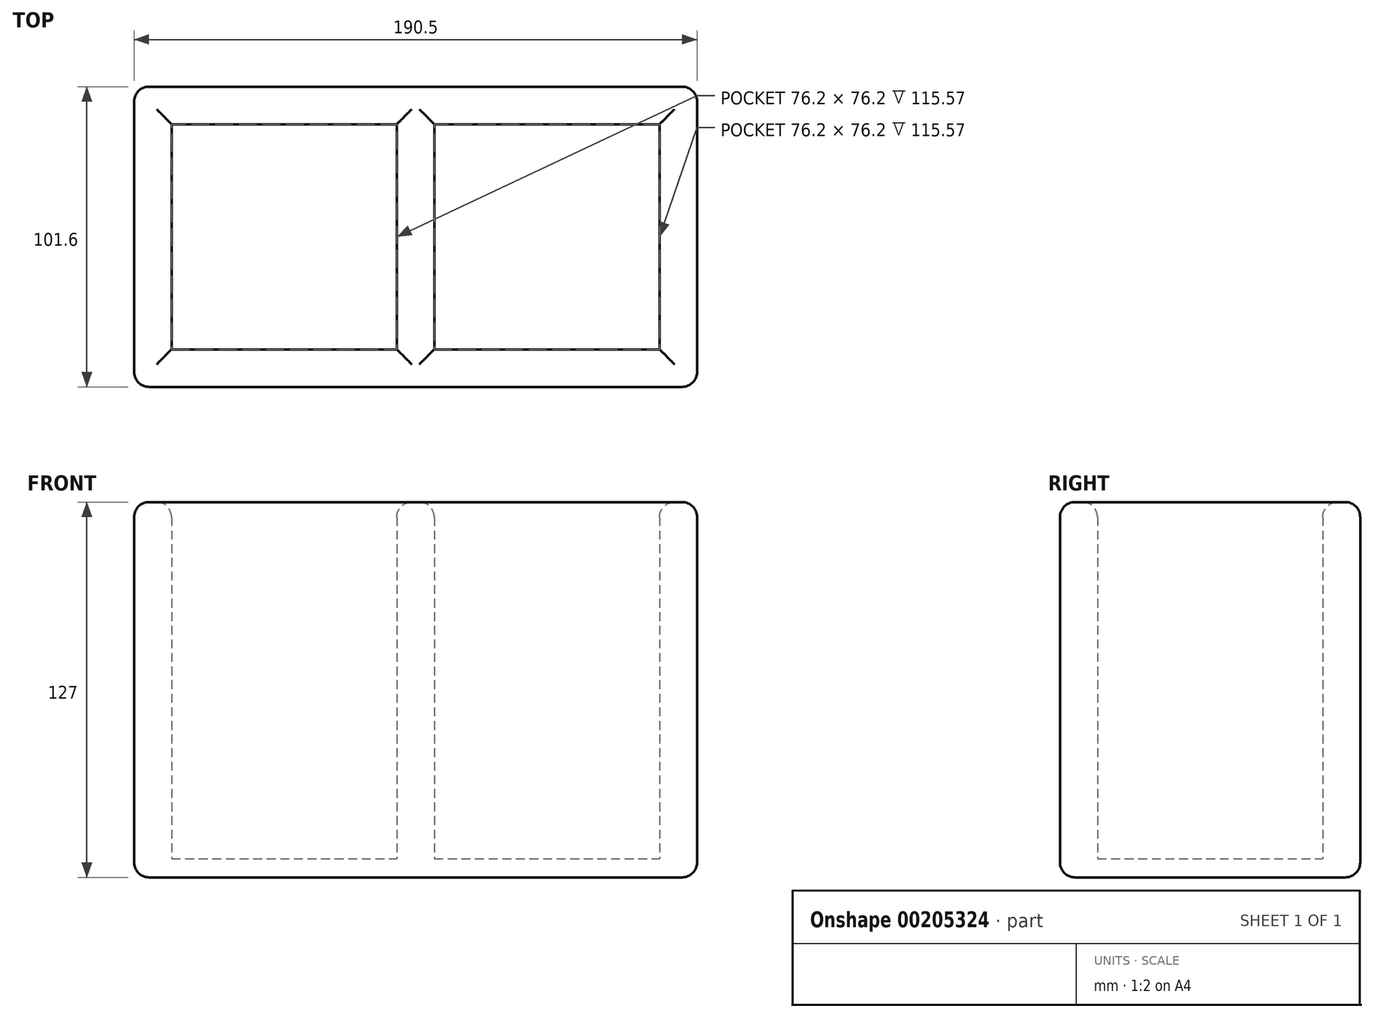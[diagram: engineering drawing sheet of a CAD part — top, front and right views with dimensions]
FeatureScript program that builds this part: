
annotation { "Feature Type Name" : "Feature", "Feature Type Description" : "" }
export const myFeature = defineFeature(function(context is Context, id is Id, definition is map)
    precondition{}
    {
        {
            var Q0;
            Q0=qCreatedBy(makeId("Top.planeOp"),FACE);
            var sketch = newSketch(context, id + "F0", { "sketchPlane" : qUnion([Q0])});
            skLineSegment(sketch, "E0.bottom", {"start": v(-95.25, -50.8) * mm, "end": v(95.25, -50.8) * mm});
            skLineSegment(sketch, "E0.top", {"start": v(-95.25, 50.8) * mm, "end": v(95.25, 50.8) * mm});
            skLineSegment(sketch, "E0.left", {"start": v(-95.25, -50.8) * mm, "end": v(-95.25, 50.8) * mm});
            skLineSegment(sketch, "E0.right", {"start": v(95.25, -50.8) * mm, "end": v(95.25, 50.8) * mm});
            skPoint(sketch, "E0.middle", {"position": v(0, 0) * mm});
            skLineSegment(sketch, "E1.0", {"start": v(-82.55, 38.1) * mm, "end": v(-6.35, 38.1) * mm});
            skLineSegment(sketch, "E1.1", {"start": v(-82.55, -38.1) * mm, "end": v(-82.55, 38.1) * mm});
            skLineSegment(sketch, "E1.2", {"start": v(-82.55, -38.1) * mm, "end": v(-6.35, -38.1) * mm});
            skLineSegment(sketch, "E1.3", {"start": v(82.55, -38.1) * mm, "end": v(82.55, 38.1) * mm});
            skPoint(sketch, "E2", {"position": v(-6.35, -38.1) * mm});
            skPoint(sketch, "E3", {"position": v(6.35, -38.1) * mm});
            skLineSegment(sketch, "E4", {"start": v(-6.35, -38.1) * mm, "end": v(-6.35, 38.1) * mm});
            skLineSegment(sketch, "E5", {"start": v(6.35, -38.1) * mm, "end": v(6.35, 38.1) * mm});
            skLineSegment(sketch, "E6.trimOffspring", {"start": v(6.35, 38.1) * mm, "end": v(82.55, 38.1) * mm});
            skLineSegment(sketch, "E7.trimOffspring", {"start": v(6.35, -38.1) * mm, "end": v(82.55, -38.1) * mm});
            skSolve(sketch);
        }
        {
            var Q0;
            Q0=makeQuery(id+"F0.imprint","IMPRINT",FACE,{"disambiguationData":[TD([[makeQuery(id+"F0.imprint","IMPRINT",EDGE,{"derivedFrom":sQuery(id+"F0.wireOp",EDGE,"E0.bottom")}),1.0]])]});
            extrude(context, id + "F1", {"entities" : qUnion([Q0]), "depth" : 127 * mm});
        }
        {
            var Q0;
            Q0=makeQuery(id+"F0.imprint","IMPRINT",FACE,{"disambiguationData":[TD([[makeQuery(id+"F0.imprint","IMPRINT",EDGE,{"derivedFrom":sQuery(id+"F0.wireOp",EDGE,"E1.0")}),-1.0]])]});
            var Q1;
            Q1=makeQuery(id+"F0.imprint","IMPRINT",FACE,{"disambiguationData":[TD([[makeQuery(id+"F0.imprint","IMPRINT",EDGE,{"derivedFrom":sQuery(id+"F0.wireOp",EDGE,"E1.3")}),1.0]])]});
            extrude(context, id + "F2", {"entities" : qUnion([Q0, Q1]), "operationType" : NewBodyOperationType.ADD, "depth" : 6.35 * mm});
        }
        {
            var Q0;
            Q0=makeQuery(id+"F1.opExtrude","CAP_EDGE",EDGE,{"disambiguationData":[OSD([sQuery(id+"F0.wireOp",EDGE,"E0.left")])],"isStart":false});
            var Q1;
            Q1=makeQuery(id+"F1.opExtrude","CAP_EDGE",EDGE,{"disambiguationData":[OSD([sQuery(id+"F0.wireOp",EDGE,"E1.1")])],"isStart":false});
            var Q2;
            Q2=makeQuery(id+"F1.opExtrude","CAP_EDGE",EDGE,{"disambiguationData":[OSD([sQuery(id+"F0.wireOp",EDGE,"E1.0")])],"isStart":false});
            var Q3;
            Q3=makeQuery(id+"F1.opExtrude","CAP_EDGE",EDGE,{"disambiguationData":[OSD([sQuery(id+"F0.wireOp",EDGE,"E4")])],"isStart":false});
            var Q4;
            Q4=makeQuery(id+"F1.opExtrude","CAP_EDGE",EDGE,{"disambiguationData":[OSD([sQuery(id+"F0.wireOp",EDGE,"E1.2")])],"isStart":false});
            var Q5;
            Q5=makeQuery(id+"F1.opExtrude","CAP_EDGE",EDGE,{"disambiguationData":[OSD([sQuery(id+"F0.wireOp",EDGE,"E5")])],"isStart":false});
            var Q6;
            Q6=makeQuery(id+"F1.opExtrude","CAP_EDGE",EDGE,{"disambiguationData":[OSD([sQuery(id+"F0.wireOp",EDGE,"E7.trimOffspring")])],"isStart":false});
            var Q7;
            Q7=makeQuery(id+"F1.opExtrude","CAP_EDGE",EDGE,{"disambiguationData":[OSD([sQuery(id+"F0.wireOp",EDGE,"E6.trimOffspring")])],"isStart":false});
            var Q8;
            Q8=makeQuery(id+"F1.opExtrude","CAP_EDGE",EDGE,{"disambiguationData":[OSD([sQuery(id+"F0.wireOp",EDGE,"E1.3")])],"isStart":false});
            var Q9;
            Q9=makeQuery(id+"F1.opExtrude","CAP_EDGE",EDGE,{"disambiguationData":[OSD([sQuery(id+"F0.wireOp",EDGE,"E0.right")])],"isStart":false});
            var Q10;
            Q10=makeQuery(id+"F1.opExtrude","CAP_EDGE",EDGE,{"disambiguationData":[OSD([sQuery(id+"F0.wireOp",EDGE,"E0.bottom")])],"isStart":false});
            var Q11;
            Q11=makeQuery(id+"F1.opExtrude","CAP_EDGE",EDGE,{"disambiguationData":[OSD([sQuery(id+"F0.wireOp",EDGE,"E0.top")])],"isStart":false});
            var Q12;
            Q12=makeQuery(id+"F1.opExtrude","SWEPT_EDGE",EDGE,{"disambiguationData":[OSD([sQuery(id+"F0.wireOp",EDGE,"E0.bottom"),sQuery(id+"F0.wireOp",EDGE,"E0.right")])]});
            var Q13;
            Q13=makeQuery(id+"F1.opExtrude","SWEPT_EDGE",EDGE,{"disambiguationData":[OSD([sQuery(id+"F0.wireOp",EDGE,"E0.top"),sQuery(id+"F0.wireOp",EDGE,"E0.right")])]});
            var Q14;
            Q14=makeQuery(id+"F1.opExtrude","SWEPT_EDGE",EDGE,{"disambiguationData":[OSD([sQuery(id+"F0.wireOp",EDGE,"E0.bottom"),sQuery(id+"F0.wireOp",EDGE,"E0.left")])]});
            var Q15;
            Q15=makeQuery(id+"F1.opExtrude","SWEPT_EDGE",EDGE,{"disambiguationData":[OSD([sQuery(id+"F0.wireOp",EDGE,"E0.top"),sQuery(id+"F0.wireOp",EDGE,"E0.left")])]});
            var Q16;
            Q16=makeQuery(id+"F1.opExtrude","CAP_EDGE",EDGE,{"disambiguationData":[OSD([sQuery(id+"F0.wireOp",EDGE,"E0.right")])],"isStart":true});
            var Q17;
            Q17=makeQuery(id+"F1.opExtrude","CAP_EDGE",EDGE,{"disambiguationData":[OSD([sQuery(id+"F0.wireOp",EDGE,"E0.bottom")])],"isStart":true});
            var Q18;
            Q18=makeQuery(id+"F1.opExtrude","CAP_EDGE",EDGE,{"disambiguationData":[OSD([sQuery(id+"F0.wireOp",EDGE,"E0.top")])],"isStart":true});
            var Q19;
            Q19=makeQuery(id+"F1.opExtrude","CAP_EDGE",EDGE,{"disambiguationData":[OSD([sQuery(id+"F0.wireOp",EDGE,"E0.left")])],"isStart":true});
            fillet(context, id + "F3", {"entities" : qUnion([Q0, Q1, Q2, Q3, Q4, Q5, Q6, Q7, Q8, Q9, Q10, Q11, Q12, Q13, Q14, Q15, Q16, Q17, Q18, Q19]), "radius" : 5.08 * mm, "tangentPropagation" : true, "allowEdgeOverflow" : false});
        }
    });
